# Revit family: LOUVER
name_source: partatom
category: Windows
revit_build: Autodesk Revit Architecture 2012 (Build: 20110916_2132(x64)
units: mm (PartAtom-declared; Revit-internal decimal feet)

## types (2) — shared parameters
Blade = <By Category>
Blade Amount = 4
Blade Distance = 300 mm
Blade Stand = <By Category>
Flashing Height = 1300 mm  [stored 4.26509 ft]
Frame Depth = 100 mm  [stored 0.328084 ft]
Frame Height = 50 mm  [stored 0.164042 ft]
Height = 1500 mm  [stored 4.92126 ft]
Rough Height = 1500 mm  [stored 4.92126 ft]
Rough Width = 4041 mm
Sill Height = 800 mm  [stored 2.62467 ft]
Top Flashing = <By Category>
Width = 4041 mm

## per-type parameters (varying)
| type | Blade Width | Half Width | Left Angle | Left x | Right Angle | Right x |
| 45 | 4241 mm | 1921 mm | 45.00° | 100 mm  [stored 0.328084 ft] | 45.00° | 100 mm  [stored 0.328084 ft] |
| 60 | 4157 mm | 1963 mm | 60.00° | 58 mm | 60.00° | 58 mm |

note: [stored X ft] marks values corroborated as IEEE doubles in the binary element streams (Revit-internal decimal feet)

## geometry (parser evidence)
native form markers: Sweep x5
no freeform markers — native parametric forms only
